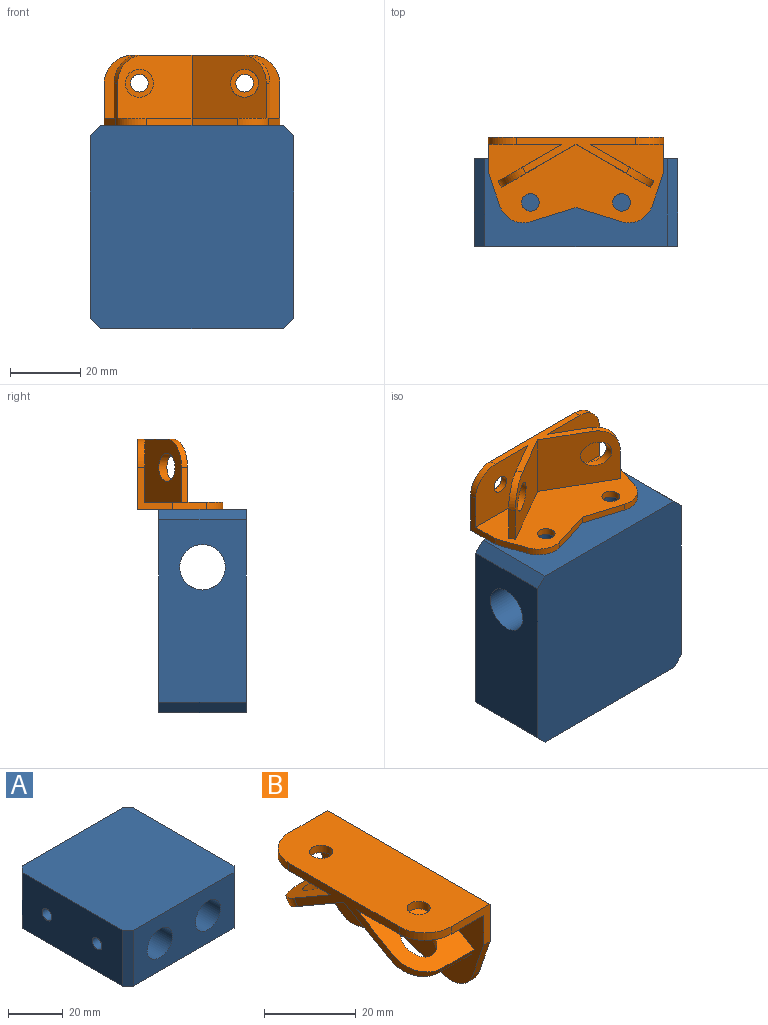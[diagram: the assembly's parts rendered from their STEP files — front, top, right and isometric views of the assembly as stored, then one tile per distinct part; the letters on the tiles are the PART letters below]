
ASSEMBLY  parts=2 mates=1
PART A: 20 faces, bbox 58x58x25 mm
  f0: plane 8x1.38mm, normal (0,-1,0), area 7.5mm2, adj f12,f14
  f1: plane 52x25mm, normal (0,1,0), area 1167.3mm2, adj f5,f6,f7,f8,f11
  f2: plane 52x25mm, normal (-1,0,0), area 1260.7mm2, adj f5,f6,f7,f10,f16,f18
  f3: plane 52x25mm, normal (0,-1,0), area 1034.5mm2, adj f5,f6,f9,f10,f11,f12
  f4: plane 52x25mm, normal (1,0,0), area 1167.3mm2, adj f5,f6,f8,f9,f14
  f5: plane 58x58mm, normal (0,0,1), area 3346mm2, adj f1,f2,f3,f4,f7,f8,f9,f10
  f6: plane 58x58mm, normal (0,0,-1), area 3346mm2, adj f1,f2,f3,f4,f7,f8,f9,f10
  f7: plane 25x3mm, normal (-0.71,0.71,0), area 106.1mm2, adj f1,f2,f5,f6
  f8: plane 25x3mm, normal (0.71,0.71,0), area 106.1mm2, adj f1,f4,f5,f6
  f9: plane 25x3mm, normal (0.71,-0.71,0), area 106.1mm2, adj f3,f4,f5,f6
  f10: plane 25x3mm, normal (-0.71,-0.71,0), area 106.1mm2, adj f2,f3,f5,f6
  f11: cylinder r=6.5mm len=58mm, axis (0,-1,0), area 2368.8mm2, adj f1,f3
  f12: cylinder r=6.5mm len=25mm, axis (0,-1,0), area 982.2mm2, adj f0,f3,f13,f14
  f13: plane 8x1.38mm, normal (0,-1,0), area 7.5mm2, adj f12,f14
  f14: cylinder r=6.5mm len=25mm, axis (1,0,0), area 887.8mm2, adj f0,f4,f12,f13,f15
  f15: plane 13x13mm, normal (1,0,0), area 132.7mm2, adj f14
  f16: cylinder r=2.5mm len=5mm, axis (-1,0,0), area 78.5mm2, adj f2,f17
  f17: plane 5x5mm, normal (-1,0,0), area 19.6mm2, adj f16
  f18: cylinder r=2.5mm len=5mm, axis (-1,0,0), area 78.5mm2, adj f2,f19
  f19: plane 5x5mm, normal (-1,0,0), area 19.6mm2, adj f18
PART B: 30 faces, bbox 20x50x24.3 mm
  f0: plane 50x22.31mm, normal (-1,0,0), area 845mm2, adj f1,f3,f4,f5,f6,f7,f8,f9
  f1: plane 12x10mm, normal (0,-1,0), area 40mm2, adj f0,f2,f10,f12,f13,f28
  f2: plane 50x20mm, normal (0,0,1), area 933.3mm2, adj f1,f3,f12,f21,f22,f23,f27,f28
  f3: plane 12x10mm, normal (0,1,0), area 40mm2, adj f0,f2,f4,f12,f14,f27
  f4: plane 9.59x3.3mm, normal (0,0.95,-0.33), area 20.3mm2, adj f0,f3,f5,f12
  f5: cylinder r=7mm len=8.67mm, axis (1,0,0), area 21.5mm2, adj f0,f4,f6,f12
  f6: plane 13.03x4mm, normal (0,-0.29,-0.96), area 27.3mm2, adj f0,f5,f7,f12
  f7: plane 13.03x4mm, normal (0,0.29,-0.96), area 27.3mm2, adj f0,f6,f8,f12
  f8: cylinder r=7mm len=8.67mm, axis (1,0,0), area 21.5mm2, adj f0,f7,f10,f12
  f9: cylinder r=2.5mm len=5mm, axis (1,0,0), area 31.4mm2, adj f0,f12
  f10: plane 9.59x3.3mm, normal (0,-0.95,-0.33), area 20.3mm2, adj f0,f1,f8,f12
  f11: cylinder r=2.5mm len=5mm, axis (1,0,0), area 31.4mm2, adj f0,f12
  f12: plane 50x24.31mm, normal (1,0,0), area 1035.9mm2, adj f1,f2,f3,f4,f5,f6,f7,f8
  f13: plane 21x18mm, normal (0,0,-1), area 344.6mm2, adj f0,f1,f20,f21,f23,f28
  f14: plane 21x18mm, normal (0,0,-1), area 344.6mm2, adj f0,f3,f15,f21,f22,f27
  f15: plane 18.19x18mm, normal (0,0.5,0.87), area 306.2mm2, adj f0,f14,f16,f21,f25,f26
  f16: plane 10x1.73mm, normal (0,0.87,-0.5), area 20mm2, adj f0,f15,f17,f26
  f17: plane 21.19x18mm, normal (0,-0.5,-0.87), area 368.6mm2, adj f0,f16,f18,f21,f25,f26
  f18: plane 21.19x18mm, normal (0,0.5,-0.87), area 368.6mm2, adj f0,f17,f19,f21,f24,f29
  f19: plane 10x1.73mm, normal (0,-0.87,-0.5), area 20mm2, adj f0,f18,f20,f29
  f20: plane 18.19x18mm, normal (0,-0.5,0.87), area 306.2mm2, adj f0,f13,f19,f21,f24,f29
  f21: plane 34x10.23mm, normal (-1,0,0), area 126.9mm2, adj f2,f13,f14,f15,f17,f18,f20,f26
  f22: cylinder r=2.5mm len=5mm, axis (0,0,1), area 31.4mm2, adj f2,f14
  f23: cylinder r=2.5mm len=5mm, axis (0,0,1), area 31.4mm2, adj f2,f13
  f24: cylinder r=4mm len=8mm, axis (0,0,1), area 58mm2, adj f18,f20
  f25: cylinder r=4mm len=8mm, axis (0,0,1), area 58mm2, adj f15,f17
  f26: cylinder r=8mm len=8mm, axis (0,0.5,0.87), area 25.1mm2, adj f15,f16,f17,f21
  f27: cylinder r=8mm len=8mm, axis (0,0,1), area 25.1mm2, adj f2,f3,f14,f21
  f28: cylinder r=8mm len=8mm, axis (0,0,-1), area 25.1mm2, adj f1,f2,f13,f21
  f29: cylinder r=8mm len=8mm, axis (0,0.5,-0.87), area 25.1mm2, adj f18,f19,f20,f21
PLACE A rot(axis=(-0.58,0.58,0.58),120deg) t=(-405.68,-51.74,-1696.61)mm
PLACE B rot(axis=(-0.58,0.58,0.58),120deg) t=(-405.68,-51.74,-1696.61)mm
MATE fastened A.f18 <-> B.f9  axis (0,0,1) through (-418.68,-39.24,-1667.61)mm
